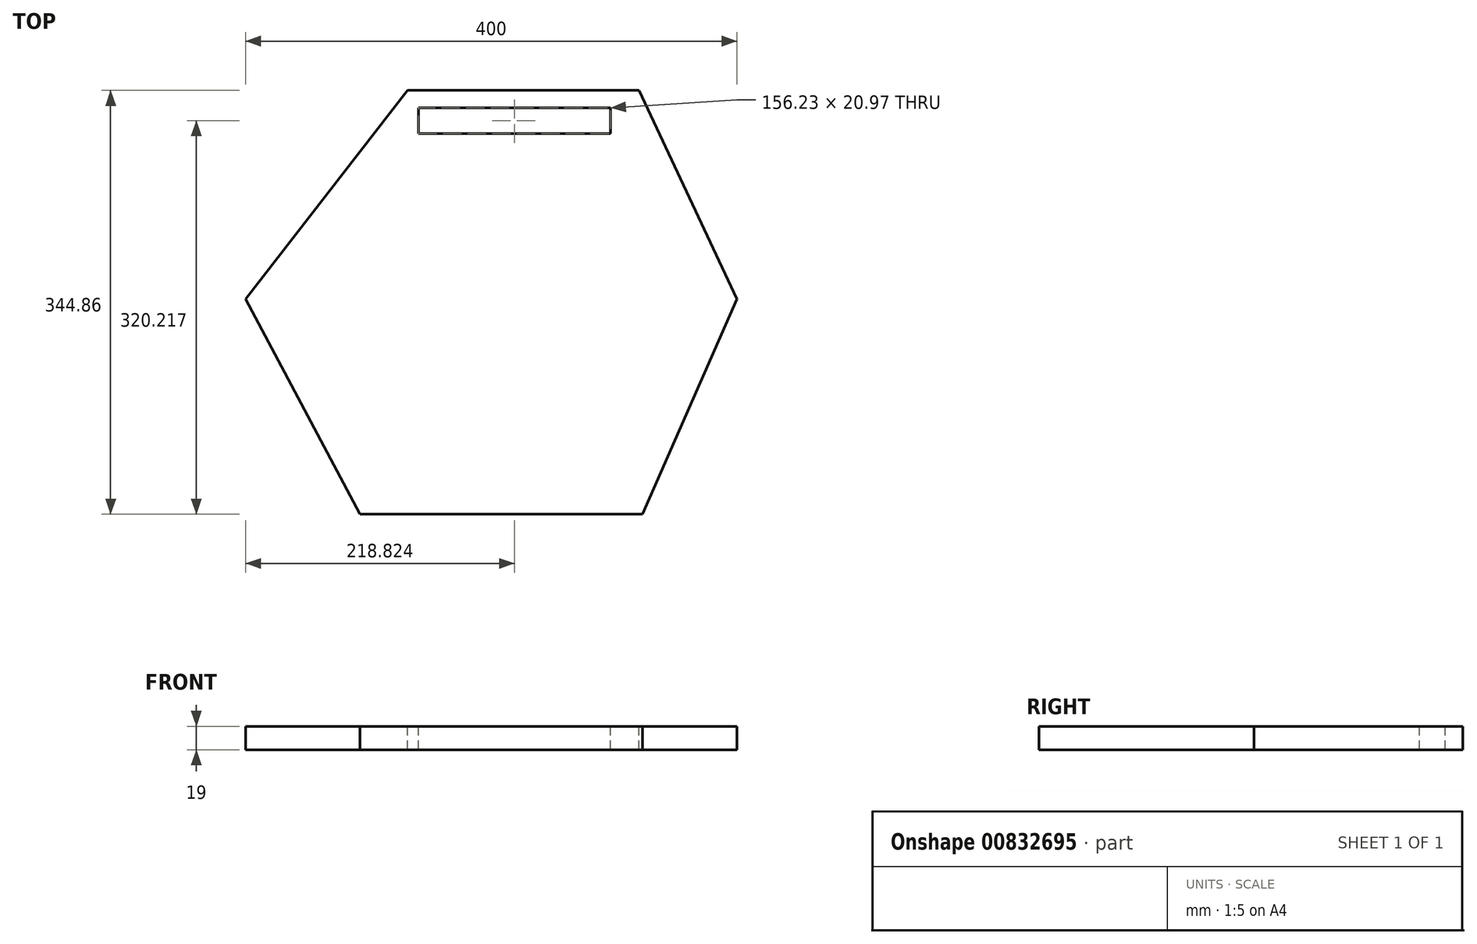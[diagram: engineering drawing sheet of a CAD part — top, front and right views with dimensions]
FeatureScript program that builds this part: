
annotation { "Feature Type Name" : "Feature", "Feature Type Description" : "" }
export const myFeature = defineFeature(function(context is Context, id is Id, definition is map)
    precondition{}
    {
        {
            var Q0;
            Q0=qCreatedBy(makeId("Top.planeOp"),FACE);
            var sketch = newSketch(context, id + "F0", { "sketchPlane" : qUnion([Q0])});
            skLineSegment(sketch, "E0.bottom", {"start": v(200, -175) * mm, "end": v(-200, -175) * mm});
            skLineSegment(sketch, "E0.top", {"start": v(200, 175) * mm, "end": v(-200, 175) * mm});
            skLineSegment(sketch, "E0.left", {"start": v(200, -175) * mm, "end": v(200, 175) * mm});
            skLineSegment(sketch, "E0.right", {"start": v(-200, -175) * mm, "end": v(-200, 175) * mm});
            skPoint(sketch, "E0.middle", {"position": v(0, 0) * mm});
            skSolve(sketch);
        }
        {
            var Q0;
            Q0 = qSketchRegion(id + "F0", true);
            extrude(context, id + "F1", {"entities" : qUnion([Q0]), "depth" : 19 * mm, "offsetDistance" : 25 * mm});
        }
        {
            var Q0;
            Q0=makeQuery(id+"F1.opExtrude","CAP_FACE",FACE,{"disambiguationData":[OSD([sQuery(id+"F0.wireOp",EDGE,"E0.bottom"),sQuery(id+"F0.wireOp",EDGE,"E0.top"),sQuery(id+"F0.wireOp",EDGE,"E0.left"),sQuery(id+"F0.wireOp",EDGE,"E0.right")])],"isStart":false});
            var sketch = newSketch(context, id + "F2", { "sketchPlane" : qUnion([Q0])});
            skLineSegment(sketch, "E1", {"start": v(-200, 0) * mm, "end": v(-68.2, 169.86) * mm});
            skLineSegment(sketch, "E2", {"start": v(-68.2, 169.86) * mm, "end": v(120, 169.86) * mm});
            skLineSegment(sketch, "E3", {"start": v(120, 169.86) * mm, "end": v(200, 0) * mm});
            skLineSegment(sketch, "E4", {"start": v(200, 0) * mm, "end": v(123.15, -175) * mm});
            skLineSegment(sketch, "E5", {"start": v(123.15, -175) * mm, "end": v(-107, -175) * mm});
            skLineSegment(sketch, "E6", {"start": v(-107, -175) * mm, "end": v(-200, 0) * mm});
            skLineSegment(sketch, "E7.bottom", {"start": v(96.94, 134.73) * mm, "end": v(-59.29, 134.73) * mm});
            skLineSegment(sketch, "E7.top", {"start": v(96.94, 155.7) * mm, "end": v(-59.29, 155.7) * mm});
            skLineSegment(sketch, "E7.left", {"start": v(96.94, 134.73) * mm, "end": v(96.94, 155.7) * mm});
            skLineSegment(sketch, "E7.right", {"start": v(-59.29, 134.73) * mm, "end": v(-59.29, 155.7) * mm});
            skPoint(sketch, "E7.middle", {"position": v(18.82, 145.22) * mm});
            skSolve(sketch);
        }
        {
            var Q0;
            Q0=makeQuery(id+"F2.imprint","IMPRINT",FACE,{"disambiguationData":[TD([[makeQuery(id+"F2.imprint","IMPRINT",EDGE,{"derivedFrom":sQuery(id+"F2.wireOp",EDGE,"E7.bottom")}),-1.0]])]});
            var Q1;
            {var subQ2=sQuery(id+"F2.wireOp",EDGE,"E1");Q1=makeQuery(id+"F2.imprint","IMPRINT",FACE,{"disambiguationData":[TD([[makeQuery(id+"F2.imprint","IMPRINT",EDGE,{"derivedFrom":subQ2}),1.0]])]});}
            var Q2;
            {var subQ0=sQuery(id+"F2.wireOp",EDGE,"E6");Q2=makeQuery(id+"F2.imprint","IMPRINT",FACE,{"disambiguationData":[TD([[makeQuery(id+"F2.imprint","IMPRINT",EDGE,{"derivedFrom":subQ0}),1.0]])]});}
            var Q3;
            {var subQ0=sQuery(id+"F2.wireOp",EDGE,"E4");Q3=makeQuery(id+"F2.imprint","IMPRINT",FACE,{"disambiguationData":[TD([[makeQuery(id+"F2.imprint","IMPRINT",EDGE,{"derivedFrom":subQ0}),1.0]])]});}
            extrude(context, id + "F3", {"entities" : qUnion([Q0, Q1, Q2, Q3]), "operationType" : NewBodyOperationType.REMOVE, "endBound" : BoundingType.THROUGH_ALL, "oppositeDirection" : true, "depth" : 25 * mm, "offsetDistance" : 25 * mm});
        }
    });
